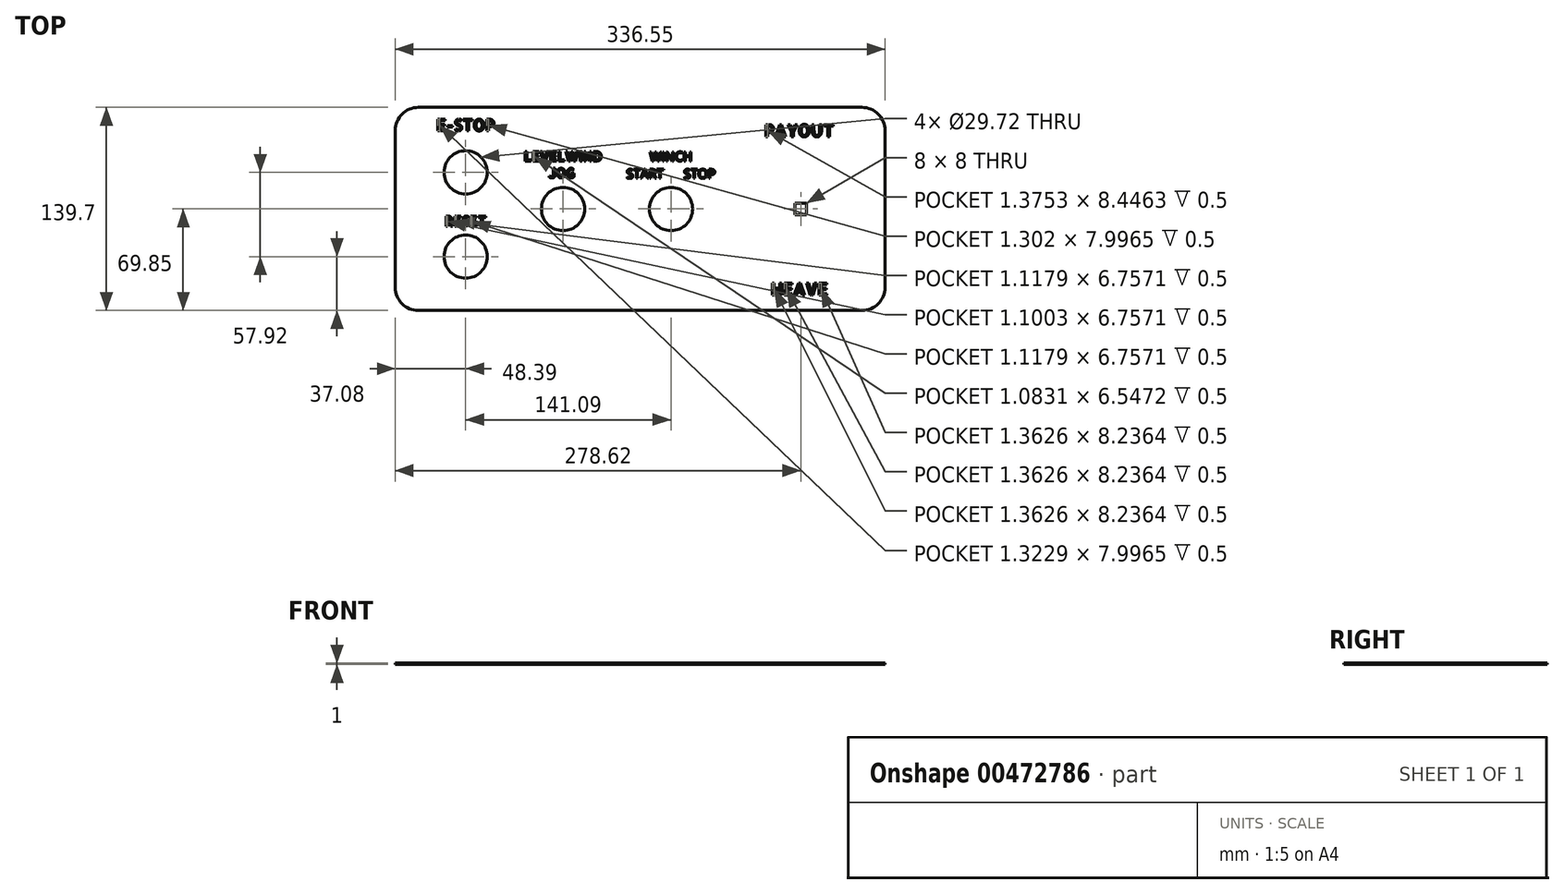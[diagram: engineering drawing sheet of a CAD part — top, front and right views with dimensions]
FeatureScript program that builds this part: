
annotation { "Feature Type Name" : "Feature", "Feature Type Description" : "" }
export const myFeature = defineFeature(function(context is Context, id is Id, definition is map)
    precondition{}
    {
        {
            var Q0;
            Q0=qCreatedBy(makeId("Top.planeOp"),FACE);
            var sketch = newSketch(context, id + "F0", { "sketchPlane" : qUnion([Q0])});
            skLineSegment(sketch, "E0.bottom", {"start": v(0, 0) * mm, "end": v(336.55, 0) * mm});
            skLineSegment(sketch, "E0.top", {"start": v(0, 139.7) * mm, "end": v(336.55, 139.7) * mm});
            skLineSegment(sketch, "E0.left", {"start": v(0, 0) * mm, "end": v(0, 139.7) * mm});
            skLineSegment(sketch, "E0.right", {"start": v(336.55, 0) * mm, "end": v(336.55, 139.7) * mm});
            skCircle(sketch, "E1", {"center": v(48.39, 95) * mm, "radius": 14.86 * mm});
            skCircle(sketch, "E2", {"center": v(48.39, 37.08) * mm, "radius": 14.86 * mm});
            skCircle(sketch, "E3", {"center": v(115.32, 69.85) * mm, "radius": 14.86 * mm});
            skCircle(sketch, "E4", {"center": v(189.48, 69.85) * mm, "radius": 14.86 * mm});
            skLineSegment(sketch, "E5.bottom", {"start": v(274.62, 73.85) * mm, "end": v(282.62, 73.85) * mm});
            skLineSegment(sketch, "E5.top", {"start": v(274.62, 65.85) * mm, "end": v(282.62, 65.85) * mm});
            skLineSegment(sketch, "E5.left", {"start": v(274.62, 73.85) * mm, "end": v(274.62, 65.85) * mm});
            skLineSegment(sketch, "E5.right", {"start": v(282.62, 73.85) * mm, "end": v(282.62, 65.85) * mm});
            skSolve(sketch);
        }
        {
            var Q0;
            Q0 = qSketchRegion(id + "F0", true);
            extrude(context, id + "F1", {"entities" : qUnion([Q0]), "depth" : 1 * mm});
        }
        {
            var Q0;
            Q0=makeQuery(id+"F1.opExtrude","SWEPT_EDGE",EDGE,{"disambiguationData":[OSD([sQuery(id+"F0.wireOp",EDGE,"E0.top"),sQuery(id+"F0.wireOp",EDGE,"E0.left")])]});
            var Q1;
            Q1=makeQuery(id+"F1.opExtrude","SWEPT_EDGE",EDGE,{"disambiguationData":[OSD([sQuery(id+"F0.wireOp",EDGE,"E0.bottom"),sQuery(id+"F0.wireOp",EDGE,"E0.left")])]});
            var Q2;
            Q2=makeQuery(id+"F1.opExtrude","SWEPT_EDGE",EDGE,{"disambiguationData":[OSD([sQuery(id+"F0.wireOp",EDGE,"E0.top"),sQuery(id+"F0.wireOp",EDGE,"E0.right")])]});
            var Q3;
            Q3=makeQuery(id+"F1.opExtrude","SWEPT_EDGE",EDGE,{"disambiguationData":[OSD([sQuery(id+"F0.wireOp",EDGE,"E0.bottom"),sQuery(id+"F0.wireOp",EDGE,"E0.right")])]});
            fillet(context, id + "F2", {"entities" : qUnion([Q0, Q1, Q2, Q3]), "radius" : 15.88 * mm, "tangentPropagation" : true, "allowEdgeOverflow" : false});
        }
        {
            var Q0;
            Q0=makeQuery(id+"F1.opExtrude","CAP_FACE",FACE,{"disambiguationData":[OSD([sQuery(id+"F0.wireOp",EDGE,"E0.bottom"),sQuery(id+"F0.wireOp",EDGE,"E0.top"),sQuery(id+"F0.wireOp",EDGE,"E0.left"),sQuery(id+"F0.wireOp",EDGE,"E0.right"),sQuery(id+"F0.wireOp",EDGE,"C8V9PFPw-KN8g-Nrg4-UwDY-NO1Dax5aquOa.bottom"),sQuery(id+"F0.wireOp",EDGE,"C8V9PFPw-KN8g-Nrg4-UwDY-NO1Dax5aquOa.top"),sQuery(id+"F0.wireOp",EDGE,"C8V9PFPw-KN8g-Nrg4-UwDY-NO1Dax5aquOa.left"),sQuery(id+"F0.wireOp",EDGE,"C8V9PFPw-KN8g-Nrg4-UwDY-NO1Dax5aquOa.right"),sQuery(id+"F0.wireOp",EDGE,"E1"),sQuery(id+"F0.wireOp",EDGE,"E2"),sQuery(id+"F0.wireOp",EDGE,"E3"),sQuery(id+"F0.wireOp",EDGE,"E4")])],"isStart":false});
            var sketch = newSketch(context, id + "F3", { "sketchPlane" : qUnion([Q0])});
            skText(sketch, "E6", { "text": "E-STOP", "fontName": "AllertaStencil-Regular.ttf"});
            skText(sketch, "E7", { "text": "RESET", "fontName": "AllertaStencil-Regular.ttf"});
            skText(sketch, "E8", { "text": "LEVELWIND\n       JOG", "fontName": "AllertaStencil-Regular.ttf"});
            skText(sketch, "E9", { "text": "       WINCH\nSTART      STOP", "fontName": "OpenSans-Regular.ttf"});
            skText(sketch, "E10", { "text": "PAYOUT", "fontName": "AllertaStencil-Regular.ttf"});
            skText(sketch, "E11", { "text": "HEAVE", "fontName": "AllertaStencil-Regular.ttf"});
            const initialGuessF3  = {"E6": [0.02823, 0.1235, 1, 0, 0.008], "E7": [0.034, 0.05808, 1, 0, 0.00676], "E8": [0.08848, 0.10285, 1, 0, 0.00655], "E9": [0.15884, 0.10285, 1, 0, 0.00634], "E10": [0.25353, 0.11947, 1, 0, 0.00845], "E11": [0.25805, 0.01069, 1, 0, 0.00824]};
            skSetInitialGuess(sketch, initialGuessF3);
            skSolve(sketch);
        }
        {
            var Q0;
            Q0 = qSketchRegion(id + "F3", true);
            extrude(context, id + "F4", {"entities" : qUnion([Q0]), "operationType" : NewBodyOperationType.REMOVE, "oppositeDirection" : true, "depth" : .5 * mm});
        }
    });
